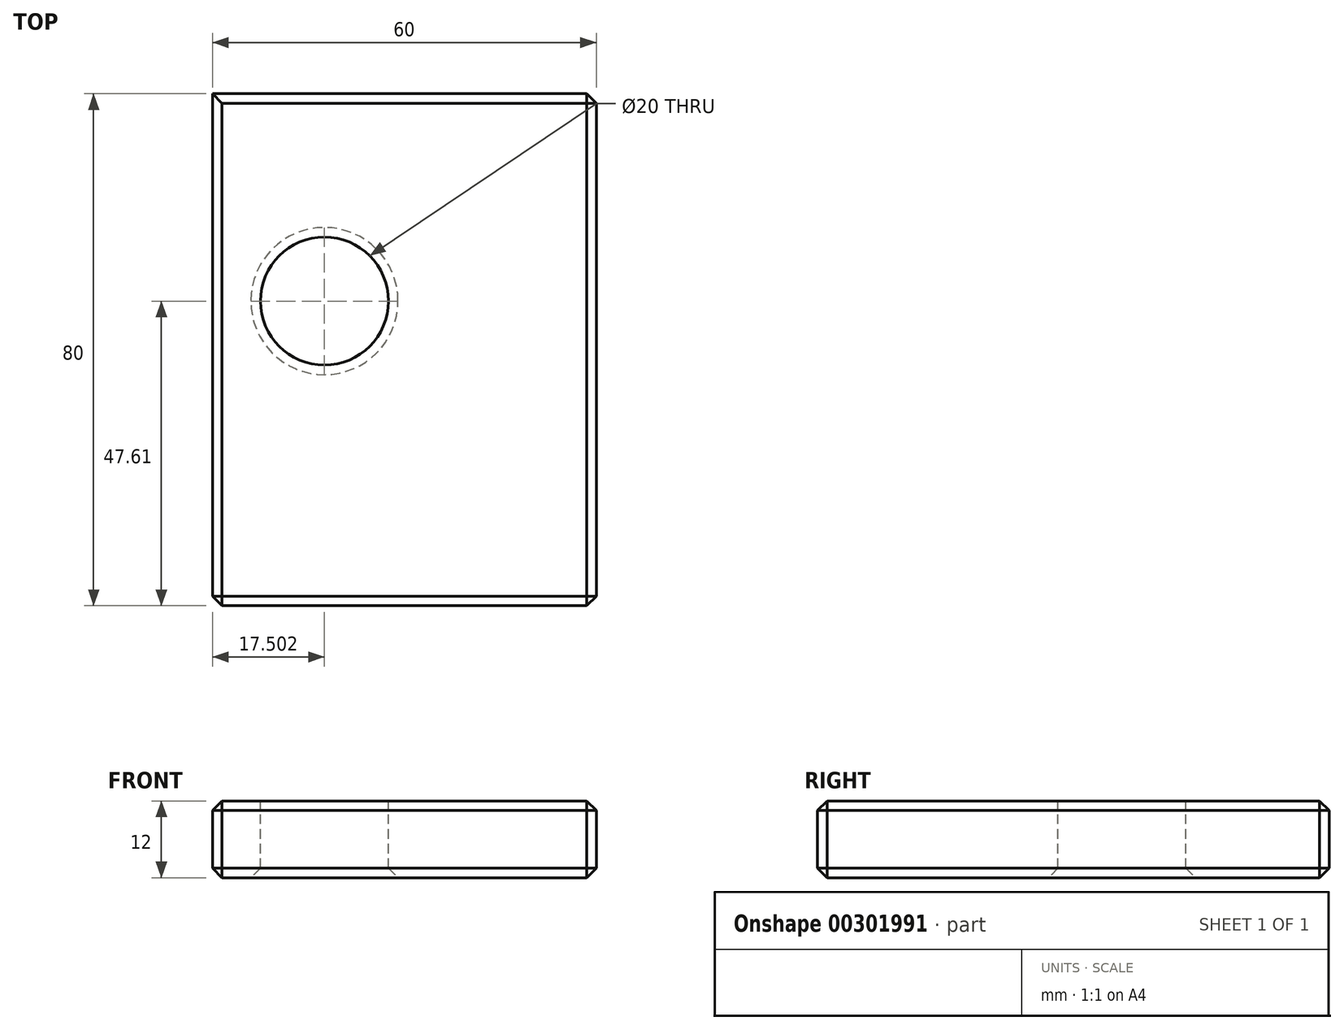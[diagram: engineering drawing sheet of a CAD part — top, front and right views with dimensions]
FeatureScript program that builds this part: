
annotation { "Feature Type Name" : "Feature", "Feature Type Description" : "" }
export const myFeature = defineFeature(function(context is Context, id is Id, definition is map)
    precondition{}
    {
        {
            var Q0;
            Q0=qCreatedBy(makeId("Top.planeOp"),FACE);
            var sketch = newSketch(context, id + "F0", { "sketchPlane" : qUnion([Q0])});
            skLineSegment(sketch, "E0.bottom", {"start": v(-31.38, 32.4) * mm, "end": v(28.62, 32.4) * mm});
            skLineSegment(sketch, "E0.top", {"start": v(-31.38, -47.6) * mm, "end": v(28.62, -47.6) * mm});
            skLineSegment(sketch, "E0.left", {"start": v(-31.38, 32.4) * mm, "end": v(-31.38, -47.6) * mm});
            skLineSegment(sketch, "E0.right", {"start": v(28.62, 32.4) * mm, "end": v(28.62, -47.6) * mm});
            skSolve(sketch);
        }
        {
            var Q0;
            Q0=makeQuery(id+"F0.imprint","IMPRINT",FACE,{"disambiguationData":[TD([[makeQuery(id+"F0.imprint","IMPRINT",EDGE,{"derivedFrom":sQuery(id+"F0.wireOp",EDGE,"E0.bottom")}),-1.0]])]});
            extrude(context, id + "F1", {"entities" : qUnion([Q0]), "depth" : 12 * mm});
        }
        {
            var Q0;
            Q0=makeQuery(id+"F1.opExtrude","CAP_FACE",FACE,{"disambiguationData":[OSD([sQuery(id+"F0.wireOp",EDGE,"E0.bottom"),sQuery(id+"F0.wireOp",EDGE,"E0.top"),sQuery(id+"F0.wireOp",EDGE,"E0.left"),sQuery(id+"F0.wireOp",EDGE,"E0.right")])],"isStart":false});
            var sketch = newSketch(context, id + "F2", { "sketchPlane" : qUnion([Q0])});
            skCircle(sketch, "E1", {"center": v(-13.88, 0) * mm, "radius": 10 * mm});
            skSolve(sketch);
        }
        {
            var Q0;
            Q0=makeQuery(id+"F2.imprint","IMPRINT",FACE,{"disambiguationData":[TD([[makeQuery(id+"F2.imprint","IMPRINT",EDGE,{"derivedFrom":sQuery(id+"F2.wireOp",EDGE,"E1")}),1.0]])]});
            extrude(context, id + "F3", {"entities" : qUnion([Q0]), "operationType" : NewBodyOperationType.REMOVE, "oppositeDirection" : true, "depth" : 25 * mm});
        }
        {
            var Q0;
            Q0=makeQuery(id+"F3.boolean.opBoolean","COPY",EDGE,{"derivedFrom":makeQuery(id+"F3.opExtrude","CAP_EDGE",EDGE,{"disambiguationData":[OSD([sQuery(id+"F2.wireOp",EDGE,"E1")])],"isStart":true})});
            var Q1;
            Q1=makeQuery(id+"F1.opExtrude","CAP_EDGE",EDGE,{"disambiguationData":[OSD([sQuery(id+"F0.wireOp",EDGE,"E0.left")])],"isStart":false});
            var Q2;
            Q2=makeQuery(id+"F1.opExtrude","CAP_EDGE",EDGE,{"disambiguationData":[OSD([sQuery(id+"F0.wireOp",EDGE,"E0.bottom")])],"isStart":false});
            var Q3;
            Q3=makeQuery(id+"F3.boolean.opBoolean","INTERSECT",EDGE,{"derivedFrom":[makeQuery(id+"F1.opExtrude","CAP_FACE",FACE,{"disambiguationData":[OSD([sQuery(id+"F0.wireOp",EDGE,"E0.bottom"),sQuery(id+"F0.wireOp",EDGE,"E0.top"),sQuery(id+"F0.wireOp",EDGE,"E0.left"),sQuery(id+"F0.wireOp",EDGE,"E0.right")])],"isStart":true}),makeQuery(id+"F3.opExtrude","SWEPT_FACE",FACE,{"disambiguationData":[OSD([sQuery(id+"F2.wireOp",EDGE,"E1")])]})]});
            var Q4;
            Q4=makeQuery(id+"F1.opExtrude","CAP_EDGE",EDGE,{"disambiguationData":[OSD([sQuery(id+"F0.wireOp",EDGE,"E0.right")])],"isStart":false});
            var Q5;
            Q5=makeQuery(id+"F1.opExtrude","CAP_EDGE",EDGE,{"disambiguationData":[OSD([sQuery(id+"F0.wireOp",EDGE,"E0.top")])],"isStart":false});
            var Q6;
            Q6=makeQuery(id+"F1.opExtrude","SWEPT_EDGE",EDGE,{"disambiguationData":[OSD([sQuery(id+"F0.wireOp",EDGE,"E0.top"),sQuery(id+"F0.wireOp",EDGE,"E0.right")])]});
            var Q7;
            Q7=makeQuery(id+"F1.opExtrude","SWEPT_EDGE",EDGE,{"disambiguationData":[OSD([sQuery(id+"F0.wireOp",EDGE,"E0.bottom"),sQuery(id+"F0.wireOp",EDGE,"E0.right")])]});
            var Q8;
            Q8=makeQuery(id+"F1.opExtrude","CAP_EDGE",EDGE,{"disambiguationData":[OSD([sQuery(id+"F0.wireOp",EDGE,"E0.bottom")])],"isStart":true});
            var Q9;
            Q9=makeQuery(id+"F1.opExtrude","CAP_EDGE",EDGE,{"disambiguationData":[OSD([sQuery(id+"F0.wireOp",EDGE,"E0.right")])],"isStart":true});
            var Q10;
            Q10=makeQuery(id+"F1.opExtrude","CAP_EDGE",EDGE,{"disambiguationData":[OSD([sQuery(id+"F0.wireOp",EDGE,"E0.top")])],"isStart":true});
            var Q11;
            Q11=makeQuery(id+"F1.opExtrude","SWEPT_EDGE",EDGE,{"disambiguationData":[OSD([sQuery(id+"F0.wireOp",EDGE,"E0.top"),sQuery(id+"F0.wireOp",EDGE,"E0.left")])]});
            var Q12;
            Q12=makeQuery(id+"F1.opExtrude","CAP_EDGE",EDGE,{"disambiguationData":[OSD([sQuery(id+"F0.wireOp",EDGE,"E0.left")])],"isStart":true});
            chamfer(context, id + "F4", {"entities" : qUnion([Q0, Q1, Q2, Q3, Q4, Q5, Q6, Q7, Q8, Q9, Q10, Q11, Q12]), "width" : 1.5 * mm, "tangentPropagation" : true});
        }
    });
